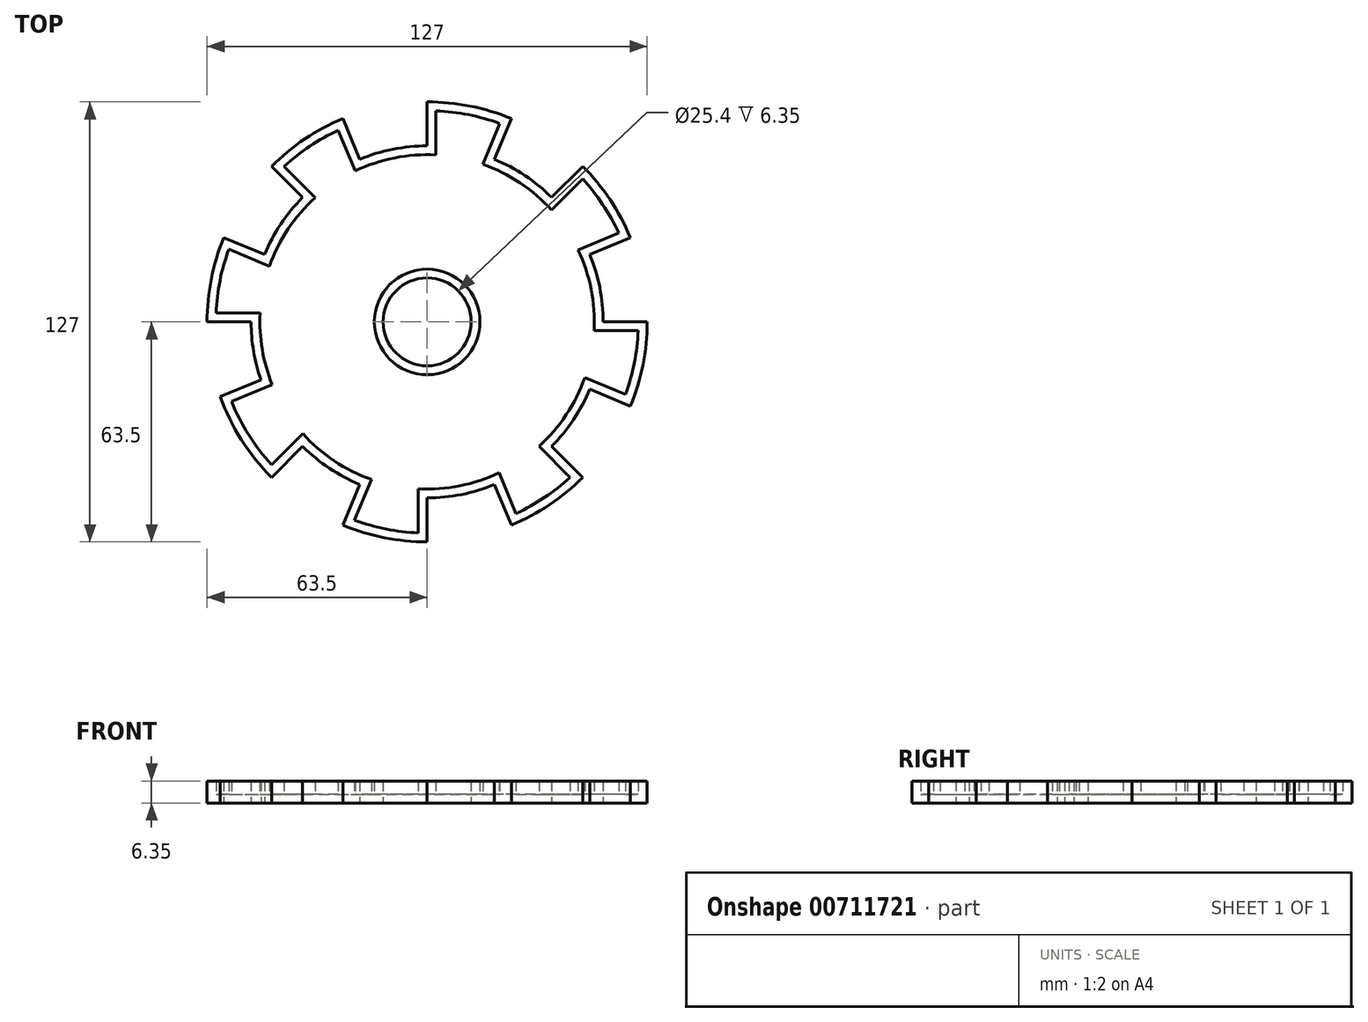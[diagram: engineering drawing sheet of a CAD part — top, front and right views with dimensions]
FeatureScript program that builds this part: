
annotation { "Feature Type Name" : "Feature", "Feature Type Description" : "" }
export const myFeature = defineFeature(function(context is Context, id is Id, definition is map)
    precondition{}
    {
        {
            var Q0;
            Q0=qCreatedBy(makeId("Top.planeOp"),FACE);
            var sketch = newSketch(context, id + "F0", { "sketchPlane" : qUnion([Q0])});
            skArc(sketch, "E0", {"start": v(-58.67, 24.3) * mm, "mid": v(-62.28, 12.39) * mm, "end": v(-63.5, 0) * mm});
            skCircle(sketch, "E1", {"center": v(0, 0) * mm, "radius": 12.7 * mm});
            skLineSegment(sketch, "E2", {"start": v(-63.5, 0) * mm, "end": v(-50.8, 0) * mm});
            skLineSegment(sketch, "E3.1.0", {"start": v(-59.72, -21.57) * mm, "end": v(-47.97, -16.7) * mm});
            skLineSegment(sketch, "E3.2.0", {"start": v(-44.9, -44.9) * mm, "end": v(-35.92, -35.92) * mm});
            skLineSegment(sketch, "E3.3.0", {"start": v(-24.3, -58.67) * mm, "end": v(-19.44, -46.93) * mm});
            skLineSegment(sketch, "E3.4.0", {"start": v(0, -63.5) * mm, "end": v(0, -50.8) * mm});
            skLineSegment(sketch, "E3.5.0", {"start": v(24.3, -58.67) * mm, "end": v(19.44, -46.93) * mm});
            skLineSegment(sketch, "E3.6.0", {"start": v(44.9, -44.9) * mm, "end": v(35.92, -35.92) * mm});
            skLineSegment(sketch, "E3.7.0", {"start": v(58.67, -24.3) * mm, "end": v(46.93, -19.44) * mm});
            skLineSegment(sketch, "E3.8.0", {"start": v(63.5, 0) * mm, "end": v(50.8, 0) * mm});
            skLineSegment(sketch, "E3.9.0", {"start": v(58.67, 24.3) * mm, "end": v(46.93, 19.44) * mm});
            skLineSegment(sketch, "E3.10.0", {"start": v(44.9, 44.9) * mm, "end": v(35.92, 35.92) * mm});
            skLineSegment(sketch, "E3.11.0", {"start": v(24.3, 58.67) * mm, "end": v(19.44, 46.93) * mm});
            skLineSegment(sketch, "E3.12.0", {"start": v(0, 63.5) * mm, "end": v(0, 50.8) * mm});
            skLineSegment(sketch, "E3.13.0", {"start": v(-24.3, 58.67) * mm, "end": v(-19.44, 46.93) * mm});
            skLineSegment(sketch, "E3.14.0", {"start": v(-44.9, 44.9) * mm, "end": v(-35.92, 35.92) * mm});
            skLineSegment(sketch, "E3.15.0", {"start": v(-58.67, 24.3) * mm, "end": v(-46.93, 19.44) * mm});
            skArc(sketch, "E4", {"start": v(-50.8, 0) * mm, "mid": v(-50.09, -8.47) * mm, "end": v(-47.97, -16.7) * mm});
            skArc(sketch, "E5.trimOffspring", {"start": v(-24.3, 58.67) * mm, "mid": v(-35.28, 52.8) * mm, "end": v(-44.9, 44.9) * mm});
            skArc(sketch, "E6.trimOffspring", {"start": v(24.3, 58.67) * mm, "mid": v(12.39, 62.28) * mm, "end": v(0, 63.5) * mm});
            skArc(sketch, "E7.trimOffspring", {"start": v(58.67, 24.3) * mm, "mid": v(52.8, 35.28) * mm, "end": v(44.9, 44.9) * mm});
            skArc(sketch, "E8.trimOffspring", {"start": v(58.67, -24.3) * mm, "mid": v(62.28, -12.39) * mm, "end": v(63.5, 0) * mm});
            skArc(sketch, "E9.trimOffspring", {"start": v(24.3, -58.67) * mm, "mid": v(35.28, -52.8) * mm, "end": v(44.9, -44.9) * mm});
            skArc(sketch, "E10.trimOffspring", {"start": v(-24.3, -58.67) * mm, "mid": v(-12.39, -62.28) * mm, "end": v(0, -63.5) * mm});
            skArc(sketch, "E11.trimOffspring", {"start": v(-59.72, -21.57) * mm, "mid": v(-53.6, -34.05) * mm, "end": v(-44.9, -44.9) * mm});
            skArc(sketch, "E12.trimOffspring", {"start": v(-35.92, 35.92) * mm, "mid": v(-42.24, 28.22) * mm, "end": v(-46.93, 19.44) * mm});
            skArc(sketch, "E13.trimOffspring", {"start": v(0, 50.8) * mm, "mid": v(-9.91, 49.82) * mm, "end": v(-19.44, 46.93) * mm});
            skArc(sketch, "E14.trimOffspring", {"start": v(35.92, 35.92) * mm, "mid": v(28.22, 42.24) * mm, "end": v(19.44, 46.93) * mm});
            skArc(sketch, "E15.trimOffspring", {"start": v(50.8, 0) * mm, "mid": v(49.82, 9.91) * mm, "end": v(46.93, 19.44) * mm});
            skArc(sketch, "E16.trimOffspring", {"start": v(35.92, -35.92) * mm, "mid": v(42.24, -28.22) * mm, "end": v(46.93, -19.44) * mm});
            skArc(sketch, "E17.trimOffspring", {"start": v(0, -50.8) * mm, "mid": v(9.91, -49.82) * mm, "end": v(19.44, -46.93) * mm});
            skArc(sketch, "E18.trimOffspring", {"start": v(-35.92, -35.92) * mm, "mid": v(-28.22, -42.24) * mm, "end": v(-19.44, -46.93) * mm});
            skSolve(sketch);
        }
        {
            var Q0;
            Q0=makeQuery(id+"F0.imprint","IMPRINT",FACE,{"disambiguationData":[TD([[makeQuery(id+"F0.imprint","IMPRINT",EDGE,{"derivedFrom":sQuery(id+"F0.wireOp",EDGE,"E0")}),1.0]])]});
            extrude(context, id + "F1", {"entities" : qUnion([Q0]), "depth" : 6.35 * mm, "offsetDistance" : 25.4 * mm});
        }
        {
            var Q0;
            Q0=makeQuery(id+"F1.opExtrude","CAP_FACE",FACE,{"disambiguationData":[OSD([sQuery(id+"F0.wireOp",EDGE,"E0"),sQuery(id+"F0.wireOp",EDGE,"E1"),sQuery(id+"F0.wireOp",EDGE,"E2"),sQuery(id+"F0.wireOp",EDGE,"E3.1.0"),sQuery(id+"F0.wireOp",EDGE,"E3.2.0"),sQuery(id+"F0.wireOp",EDGE,"E3.3.0"),sQuery(id+"F0.wireOp",EDGE,"E3.4.0"),sQuery(id+"F0.wireOp",EDGE,"E3.5.0"),sQuery(id+"F0.wireOp",EDGE,"E3.6.0"),sQuery(id+"F0.wireOp",EDGE,"E3.7.0"),sQuery(id+"F0.wireOp",EDGE,"E3.8.0"),sQuery(id+"F0.wireOp",EDGE,"E3.9.0"),sQuery(id+"F0.wireOp",EDGE,"E3.10.0"),sQuery(id+"F0.wireOp",EDGE,"E3.11.0"),sQuery(id+"F0.wireOp",EDGE,"E3.12.0"),sQuery(id+"F0.wireOp",EDGE,"E3.13.0"),sQuery(id+"F0.wireOp",EDGE,"E3.14.0"),sQuery(id+"F0.wireOp",EDGE,"E3.15.0"),sQuery(id+"F0.wireOp",EDGE,"E4"),sQuery(id+"F0.wireOp",EDGE,"E5.trimOffspring"),sQuery(id+"F0.wireOp",EDGE,"E6.trimOffspring"),sQuery(id+"F0.wireOp",EDGE,"E7.trimOffspring"),sQuery(id+"F0.wireOp",EDGE,"E8.trimOffspring"),sQuery(id+"F0.wireOp",EDGE,"E9.trimOffspring"),sQuery(id+"F0.wireOp",EDGE,"E10.trimOffspring"),sQuery(id+"F0.wireOp",EDGE,"E11.trimOffspring"),sQuery(id+"F0.wireOp",EDGE,"E12.trimOffspring"),sQuery(id+"F0.wireOp",EDGE,"E13.trimOffspring"),sQuery(id+"F0.wireOp",EDGE,"E14.trimOffspring"),sQuery(id+"F0.wireOp",EDGE,"E15.trimOffspring"),sQuery(id+"F0.wireOp",EDGE,"E16.trimOffspring"),sQuery(id+"F0.wireOp",EDGE,"E17.trimOffspring"),sQuery(id+"F0.wireOp",EDGE,"E18.trimOffspring")])],"isStart":false});
            shell(context, id + "F2", {"entities" : qUnion([Q0]), "thickness" : 2.54 * mm});
        }
    });
